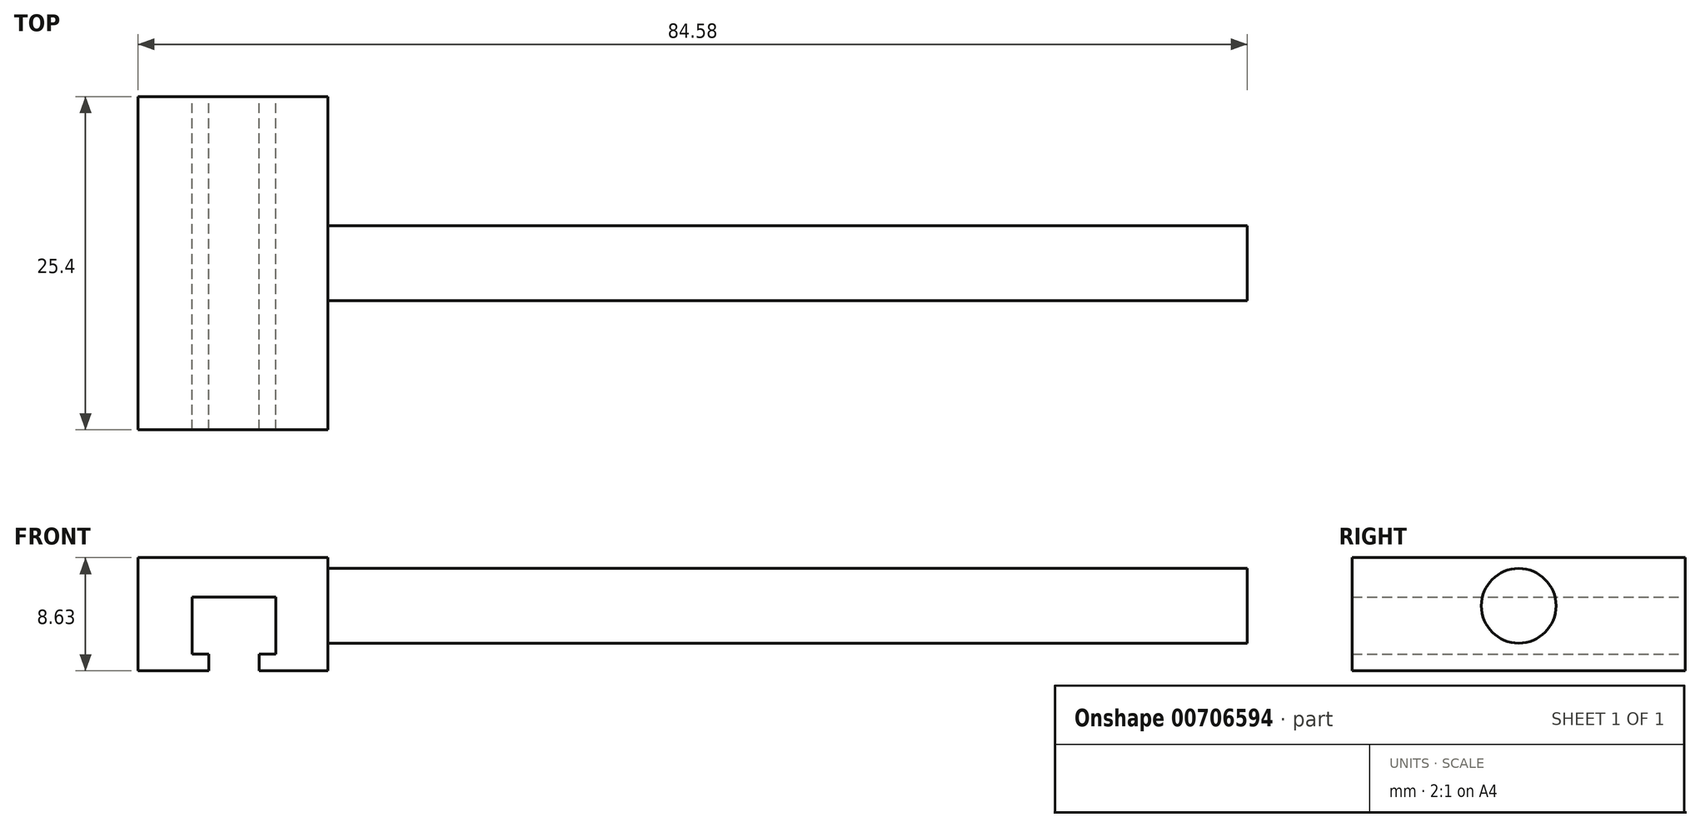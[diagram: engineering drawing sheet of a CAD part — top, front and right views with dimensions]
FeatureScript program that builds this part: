
annotation { "Feature Type Name" : "Feature", "Feature Type Description" : "" }
export const myFeature = defineFeature(function(context is Context, id is Id, definition is map)
    precondition{}
    {
        {
            var Q0;
            Q0=qCreatedBy(makeId("Front.planeOp"),FACE);
            var sketch = newSketch(context, id + "F0", { "sketchPlane" : qUnion([Q0])});
            skLineSegment(sketch, "E0", {"start": v(0, 0) * mm, "end": v(0, 11.93) * mm});
            skLineSegment(sketch, "E1", {"start": v(0, 11.93) * mm, "end": v(14.47, 11.93) * mm});
            skLineSegment(sketch, "E2", {"start": v(14.47, 11.93) * mm, "end": v(14.47, 0) * mm});
            skLineSegment(sketch, "E3", {"start": v(4.11, 8.91) * mm, "end": v(10.5, 8.91) * mm});
            skLineSegment(sketch, "E4", {"start": v(10.5, 8.91) * mm, "end": v(10.5, 0) * mm});
            skLineSegment(sketch, "E5", {"start": v(10.5, 0) * mm, "end": v(14.47, 0) * mm});
            skLineSegment(sketch, "E6", {"start": v(4.11, 8.91) * mm, "end": v(4.11, 0) * mm});
            skLineSegment(sketch, "E7", {"start": v(4.11, 0) * mm, "end": v(0, 0) * mm});
            skSolve(sketch);
        }
        {
            var Q0;
            Q0=makeQuery(id+"F0.imprint","IMPRINT",FACE,{"disambiguationData":[TD([[makeQuery(id+"F0.imprint","IMPRINT",EDGE,{"derivedFrom":sQuery(id+"F0.wireOp",EDGE,"E0")}),-1.0]])]});
            extrude(context, id + "F1", {"entities" : qUnion([Q0]), "depth" : 25.4 * mm, "offsetDistance" : 25.4 * mm});
        }
        {
            var Q0;
            Q0=makeQuery(id+"F1.opExtrude","SWEPT_FACE",FACE,{"disambiguationData":[OSD([sQuery(id+"F0.wireOp",EDGE,"E7")])]});
            var Q1;
            Q1=makeQuery(id+"F1.opExtrude","SWEPT_FACE",FACE,{"disambiguationData":[OSD([sQuery(id+"F0.wireOp",EDGE,"E5")])]});
            extrude(context, id + "F2", {"entities" : qUnion([Q0, Q1]), "operationType" : NewBodyOperationType.REMOVE, "oppositeDirection" : true, "depth" : 4.57 * mm, "offsetDistance" : 25.4 * mm});
        }
        {
            var Q0;
            Q0=makeQuery(id+"F1.opExtrude","SWEPT_FACE",FACE,{"disambiguationData":[OSD([sQuery(id+"F0.wireOp",EDGE,"E2")])]});
            var sketch = newSketch(context, id + "F3", { "sketchPlane" : qUnion([Q0])});
            skCircle(sketch, "E8", {"center": v(-12.7, 8.25) * mm, "radius": 2.85 * mm});
            skPoint(sketch, "E8.centerSnap0", {"position": v(-12.7, 11.93) * mm});
            skPoint(sketch, "E8.centerSnap1", {"position": v(0, 8.25) * mm});
            skSolve(sketch);
        }
        {
            var Q0;
            Q0=makeQuery(id+"F3.imprint","IMPRINT",FACE,{"disambiguationData":[TD([[makeQuery(id+"F3.imprint","IMPRINT",EDGE,{"derivedFrom":sQuery(id+"F3.wireOp",EDGE,"E8")}),1.0]])]});
            extrude(context, id + "F4", {"entities" : qUnion([Q0]), "operationType" : NewBodyOperationType.ADD, "depth" : 70.1 * mm, "offsetDistance" : 25.4 * mm});
        }
        {
            var Q0;
            Q0=makeQuery(id+"F2.boolean.opBoolean","COPY",FACE,{"derivedFrom":makeQuery(id+"F2.opExtrude","CAP_FACE",FACE,{"disambiguationData":[OSD([sQuery(id+"F0.wireOp",EDGE,"E5")])],"isStart":false})});
            var Q1;
            Q1=makeQuery(id+"F2.boolean.opBoolean","COPY",FACE,{"derivedFrom":makeQuery(id+"F2.opExtrude","CAP_FACE",FACE,{"disambiguationData":[OSD([sQuery(id+"F0.wireOp",EDGE,"E7")])],"isStart":false})});
            extrude(context, id + "F5", {"entities" : qUnion([Q0, Q1]), "operationType" : NewBodyOperationType.ADD, "depth" : 1.27 * mm, "offsetDistance" : 25.4 * mm});
        }
        {
            var Q0;
            {var subQ0=sQuery(id+"F0.wireOp",EDGE,"E4");Q0=makeQuery(id+"F5.boolean.opBoolean","MERGE",FACE,{"derivedFrom":[makeQuery(id+"F1.opExtrude","SWEPT_FACE",FACE,{"disambiguationData":[OSD([subQ0])]}),makeQuery(id+"F5.opExtrude","SWEPT_FACE",FACE,{"disambiguationData":[OSD([subQ0,sQuery(id+"F0.wireOp",EDGE,"E5")])]})]});}
            var sketch = newSketch(context, id + "F6", { "sketchPlane" : qUnion([Q0])});
            skLineSegment(sketch, "E9.bottom", {"start": v(25.4, 3.3) * mm, "end": v(0, 3.3) * mm});
            skLineSegment(sketch, "E9.top", {"start": v(25.4, 4.56) * mm, "end": v(0, 4.56) * mm});
            skLineSegment(sketch, "E9.left", {"start": v(25.4, 3.3) * mm, "end": v(25.4, 4.56) * mm});
            skLineSegment(sketch, "E9.right", {"start": v(0, 3.3) * mm, "end": v(0, 4.56) * mm});
            skSolve(sketch);
        }
        {
            var Q0;
            {var subQ0=sQuery(id+"F0.wireOp",EDGE,"E6");Q0=makeQuery(id+"F5.boolean.opBoolean","MERGE",FACE,{"derivedFrom":[makeQuery(id+"F1.opExtrude","SWEPT_FACE",FACE,{"disambiguationData":[OSD([subQ0])]}),makeQuery(id+"F5.opExtrude","SWEPT_FACE",FACE,{"disambiguationData":[OSD([subQ0,sQuery(id+"F0.wireOp",EDGE,"E7")])]})]});}
            var sketch = newSketch(context, id + "F7", { "sketchPlane" : qUnion([Q0])});
            skLineSegment(sketch, "E10.bottom", {"start": v(-25.4, 3.3) * mm, "end": v(0, 3.3) * mm});
            skLineSegment(sketch, "E10.top", {"start": v(-25.4, 4.56) * mm, "end": v(0, 4.56) * mm});
            skLineSegment(sketch, "E10.left", {"start": v(-25.4, 3.3) * mm, "end": v(-25.4, 4.56) * mm});
            skLineSegment(sketch, "E10.right", {"start": v(0, 3.3) * mm, "end": v(0, 4.56) * mm});
            skSolve(sketch);
        }
        {
            var Q0;
            Q0=makeQuery(id+"F6.imprint","IMPRINT",FACE,{"disambiguationData":[TD([[makeQuery(id+"F6.imprint","IMPRINT",EDGE,{"derivedFrom":sQuery(id+"F6.wireOp",EDGE,"E9.bottom")}),-1.0]])]});
            extrude(context, id + "F8", {"entities" : qUnion([Q0]), "operationType" : NewBodyOperationType.ADD, "depth" : 1.27 * mm, "offsetDistance" : 25.4 * mm});
        }
        {
            var Q0;
            Q0=makeQuery(id+"F7.imprint","IMPRINT",FACE,{"disambiguationData":[TD([[makeQuery(id+"F7.imprint","IMPRINT",EDGE,{"derivedFrom":sQuery(id+"F7.wireOp",EDGE,"E10.bottom")}),1.0]])]});
            extrude(context, id + "F9", {"entities" : qUnion([Q0]), "operationType" : NewBodyOperationType.ADD, "depth" : 1.27 * mm, "offsetDistance" : 25.4 * mm});
        }
    });
